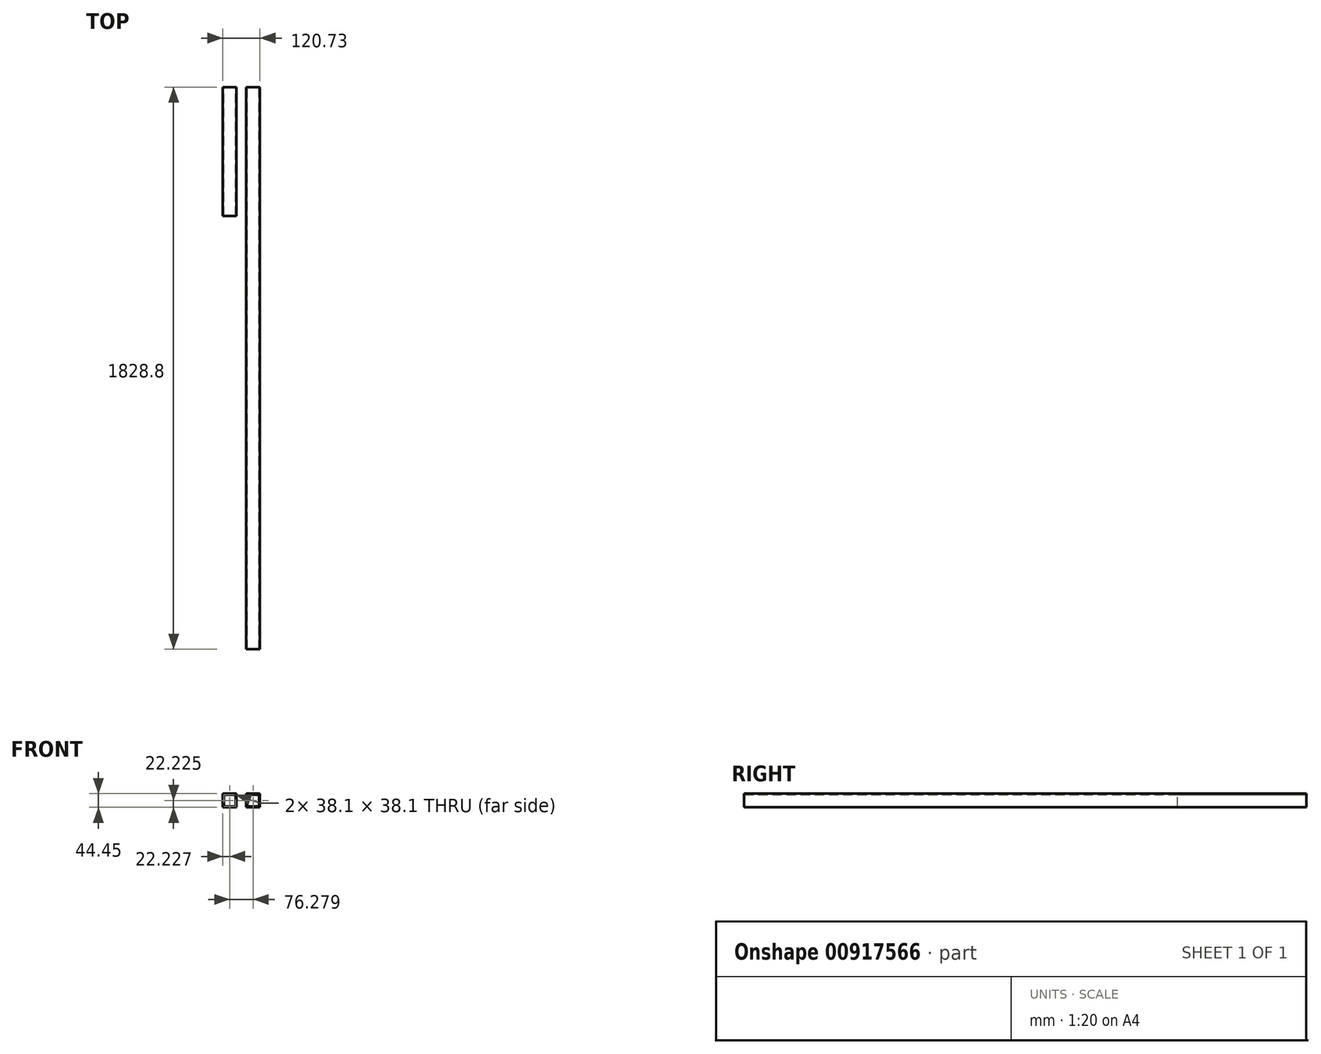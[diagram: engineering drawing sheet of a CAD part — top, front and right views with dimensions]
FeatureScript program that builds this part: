
annotation { "Feature Type Name" : "Feature", "Feature Type Description" : "" }
export const myFeature = defineFeature(function(context is Context, id is Id, definition is map)
    precondition{}
    {
        {
            var Q0;
            Q0=qCreatedBy(makeId("Front.planeOp"),FACE);
            var sketch = newSketch(context, id + "F0", { "sketchPlane" : qUnion([Q0])});
            skLineSegment(sketch, "E0.bottom", {"start": v(0, 0) * mm, "end": v(44.45, 0) * mm});
            skLineSegment(sketch, "E0.top", {"start": v(0, 44.45) * mm, "end": v(44.45, 44.45) * mm});
            skLineSegment(sketch, "E0.left", {"start": v(0, 0) * mm, "end": v(0, 44.45) * mm});
            skLineSegment(sketch, "E0.right", {"start": v(44.45, 0) * mm, "end": v(44.45, 44.45) * mm});
            skLineSegment(sketch, "E1.0", {"start": v(3.18, 3.18) * mm, "end": v(41.28, 3.18) * mm});
            skLineSegment(sketch, "E1.1", {"start": v(3.17, 3.18) * mm, "end": v(3.17, 41.28) * mm});
            skLineSegment(sketch, "E1.2", {"start": v(3.17, 41.28) * mm, "end": v(41.27, 41.28) * mm});
            skLineSegment(sketch, "E1.3", {"start": v(41.28, 3.18) * mm, "end": v(41.27, 41.28) * mm});
            skSolve(sketch);
        }
        {
            var Q0;
            Q0=makeQuery(id+"F0.imprint","IMPRINT",FACE,{"disambiguationData":[TD([[makeQuery(id+"F0.imprint","IMPRINT",EDGE,{"derivedFrom":sQuery(id+"F0.wireOp",EDGE,"E0.bottom")}),1.0]])]});
            extrude(context, id + "F1", {"entities" : qUnion([Q0]), "depth" : 1828.8 * mm, "offsetDistance" : 25.4 * mm});
        }
        {
            var Q0;
            Q0=qCreatedBy(makeId("Front.planeOp"),FACE);
            var sketch = newSketch(context, id + "F2", { "sketchPlane" : qUnion([Q0])});
            skLineSegment(sketch, "E2.bottom", {"start": v(-31.83, 0) * mm, "end": v(-76.28, 0) * mm});
            skLineSegment(sketch, "E2.top", {"start": v(-31.83, 44.45) * mm, "end": v(-76.28, 44.45) * mm});
            skLineSegment(sketch, "E2.left", {"start": v(-31.83, 0) * mm, "end": v(-31.83, 44.45) * mm});
            skLineSegment(sketch, "E2.right", {"start": v(-76.28, 0) * mm, "end": v(-76.28, 44.45) * mm});
            skLineSegment(sketch, "E3.0", {"start": v(-35, 41.28) * mm, "end": v(-73.1, 41.28) * mm});
            skLineSegment(sketch, "E3.1", {"start": v(-35, 3.18) * mm, "end": v(-35, 41.28) * mm});
            skLineSegment(sketch, "E3.2", {"start": v(-35, 3.17) * mm, "end": v(-73.1, 3.17) * mm});
            skLineSegment(sketch, "E3.3", {"start": v(-73.1, 3.17) * mm, "end": v(-73.1, 41.28) * mm});
            skSolve(sketch);
        }
        {
            var Q0;
            Q0=makeQuery(id+"F2.imprint","IMPRINT",FACE,{"disambiguationData":[TD([[makeQuery(id+"F2.imprint","IMPRINT",EDGE,{"derivedFrom":sQuery(id+"F2.wireOp",EDGE,"E2.bottom")}),-1.0]])]});
            extrude(context, id + "F3", {"entities" : qUnion([Q0]), "depth" : 419.1 * mm, "offsetDistance" : 25.4 * mm});
        }
    });
